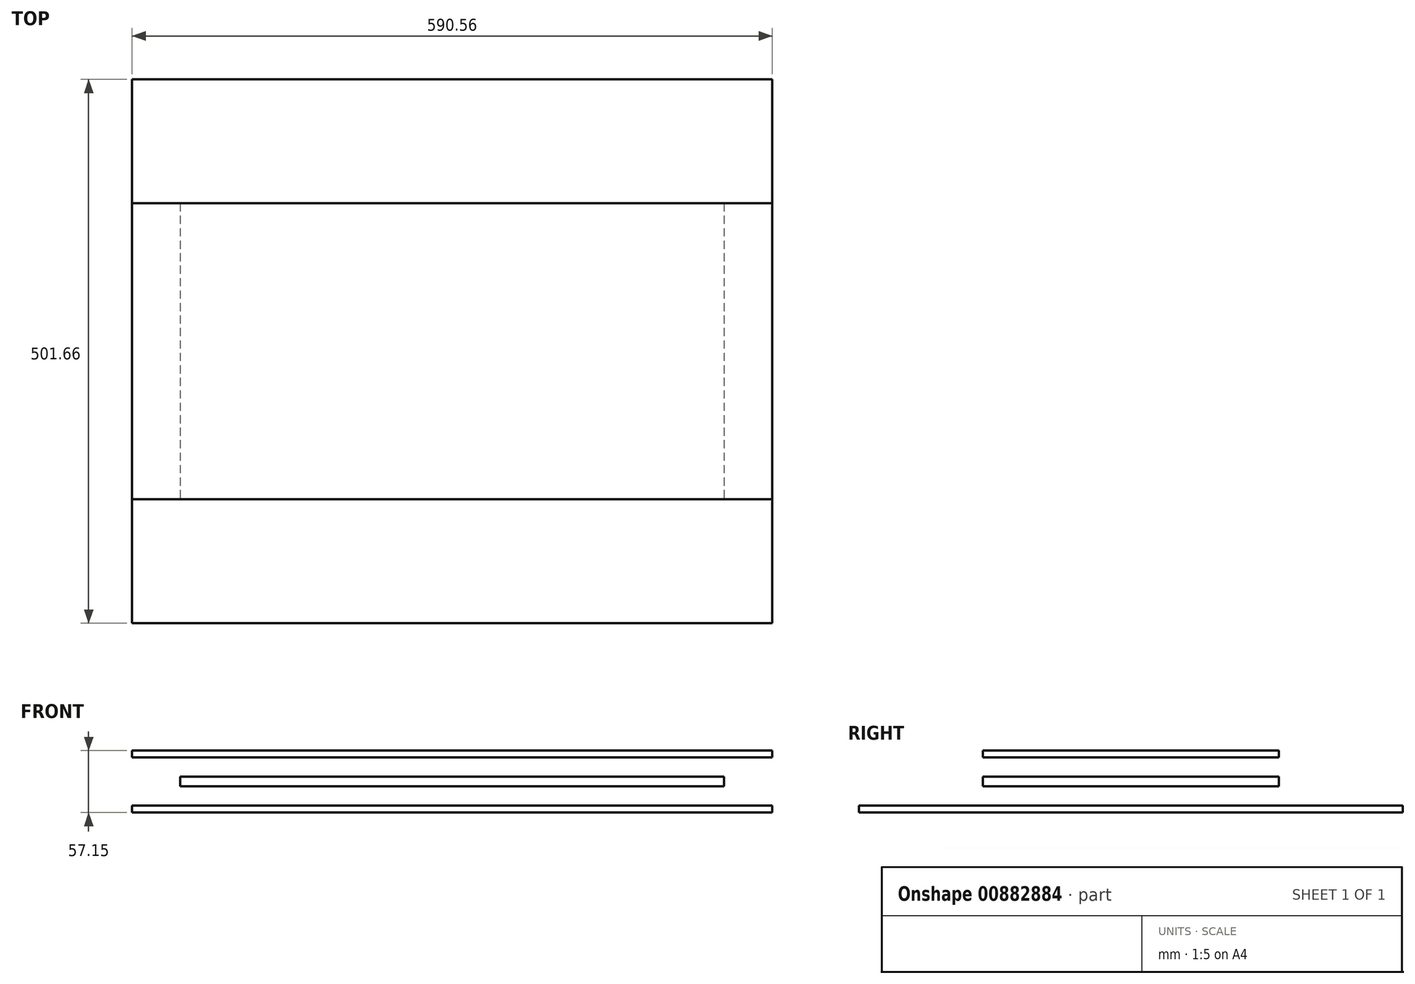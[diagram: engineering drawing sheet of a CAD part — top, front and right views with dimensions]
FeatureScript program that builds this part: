
annotation { "Feature Type Name" : "Feature", "Feature Type Description" : "" }
export const myFeature = defineFeature(function(context is Context, id is Id, definition is map)
    precondition{}
    {
        {
            var Q0;
            Q0=qCreatedBy(makeId("Top.planeOp"),FACE);
            cPlane(context, id + "F0", {"entities" : qUnion([Q0]), "cplaneType" : CPlaneType.OFFSET, "offset" : 25.4 * mm, "width" : 152.4 * mm, "height" : 152.4 * mm});
        }
        {
            var Q0;
            Q0=qCreatedBy(makeId("Top.planeOp"),FACE);
            cPlane(context, id + "F1", {"entities" : qUnion([Q0]), "cplaneType" : CPlaneType.OFFSET, "offset" : 50.8 * mm, "width" : 152.4 * mm, "height" : 152.4 * mm});
        }
        {
            var Q0;
            Q0=qCreatedBy(makeId("Top.planeOp"),FACE);
            var sketch = newSketch(context, id + "F2", { "sketchPlane" : qUnion([Q0])});
            skLineSegment(sketch, "E0.bottom", {"start": v(295.28, 250.83) * mm, "end": v(-295.28, 250.83) * mm});
            skLineSegment(sketch, "E0.top", {"start": v(295.27, -250.82) * mm, "end": v(-295.28, -250.82) * mm});
            skLineSegment(sketch, "E0.left", {"start": v(295.28, 250.83) * mm, "end": v(295.27, -250.82) * mm});
            skLineSegment(sketch, "E0.right", {"start": v(-295.28, 250.83) * mm, "end": v(-295.28, -250.82) * mm});
            skPoint(sketch, "E0.middle", {"position": v(0, 0) * mm});
            skSolve(sketch);
        }
        {
            var Q0;
            Q0=makeQuery(id+"F2.imprint","IMPRINT",FACE,{"disambiguationData":[TD([[makeQuery(id+"F2.imprint","IMPRINT",EDGE,{"derivedFrom":sQuery(id+"F2.wireOp",EDGE,"E0.bottom")}),1.0]])]});
            extrude(context, id + "F3", {"entities" : qUnion([Q0]), "endBound" : BoundingType.SYMMETRIC, "depth" : 6.35 * mm, "offsetDistance" : 25.4 * mm});
        }
        {
            var Q0;
            Q0=qCreatedBy(id+"F0.planeOp",FACE);
            var sketch = newSketch(context, id + "F4", { "sketchPlane" : qUnion([Q0])});
            skPoint(sketch, "E1.0", {"position": v(0, 0) * mm});
            skLineSegment(sketch, "E2.bottom", {"start": v(250.83, 136.53) * mm, "end": v(-250.82, 136.53) * mm});
            skLineSegment(sketch, "E2.top", {"start": v(250.82, -136.53) * mm, "end": v(-250.83, -136.53) * mm});
            skLineSegment(sketch, "E2.left", {"start": v(250.83, 136.53) * mm, "end": v(250.82, -136.53) * mm});
            skLineSegment(sketch, "E2.right", {"start": v(-250.82, 136.53) * mm, "end": v(-250.83, -136.53) * mm});
            skSolve(sketch);
        }
        {
            var Q0;
            Q0=makeQuery(id+"F4.imprint","IMPRINT",FACE,{"disambiguationData":[TD([[makeQuery(id+"F4.imprint","IMPRINT",EDGE,{"derivedFrom":sQuery(id+"F4.wireOp",EDGE,"E2.bottom")}),1.0]])]});
            extrude(context, id + "F5", {"entities" : qUnion([Q0]), "endBound" : BoundingType.SYMMETRIC, "depth" : 8.9 * mm, "offsetDistance" : 25.4 * mm});
        }
        {
            var Q0;
            Q0=qCreatedBy(id+"F1.planeOp",FACE);
            var sketch = newSketch(context, id + "F6", { "sketchPlane" : qUnion([Q0])});
            skPoint(sketch, "E3.0", {"position": v(0, 0) * mm});
            skLineSegment(sketch, "E4.bottom", {"start": v(295.28, 136.53) * mm, "end": v(-295.28, 136.53) * mm});
            skLineSegment(sketch, "E4.top", {"start": v(295.28, -136.53) * mm, "end": v(-295.27, -136.53) * mm});
            skLineSegment(sketch, "E4.left", {"start": v(295.28, 136.53) * mm, "end": v(295.28, -136.53) * mm});
            skLineSegment(sketch, "E4.right", {"start": v(-295.28, 136.53) * mm, "end": v(-295.28, -136.53) * mm});
            skSolve(sketch);
        }
        {
            var Q0;
            Q0=makeQuery(id+"F6.imprint","IMPRINT",FACE,{"disambiguationData":[TD([[makeQuery(id+"F6.imprint","IMPRINT",EDGE,{"derivedFrom":sQuery(id+"F6.wireOp",EDGE,"E4.bottom")}),1.0]])]});
            extrude(context, id + "F7", {"entities" : qUnion([Q0]), "endBound" : BoundingType.SYMMETRIC, "depth" : 6.35 * mm, "offsetDistance" : 25.4 * mm});
        }
    });
